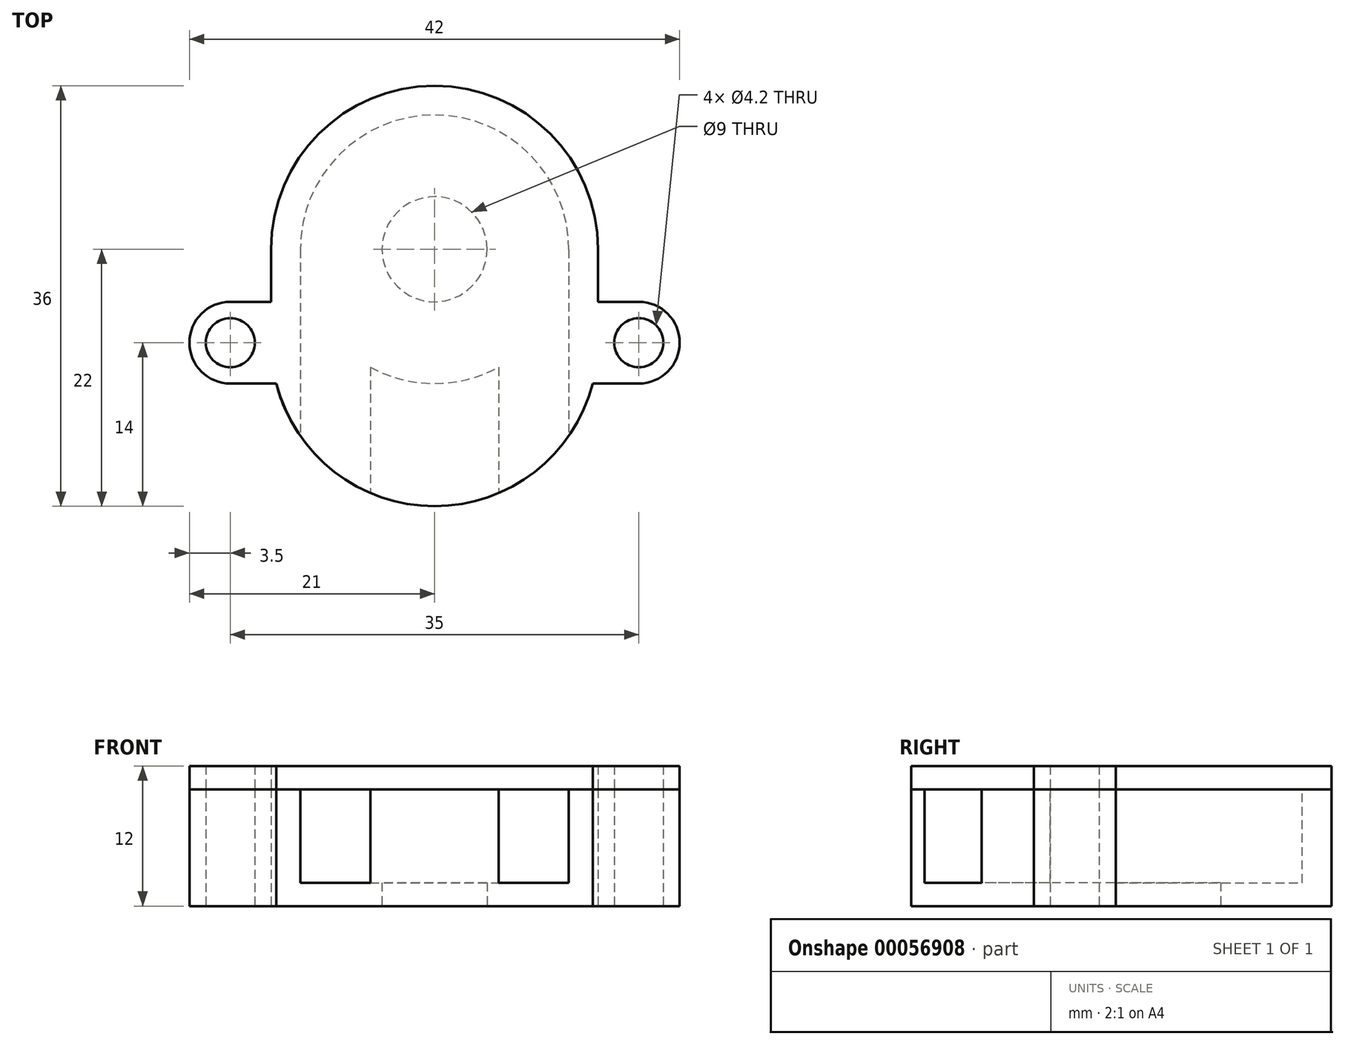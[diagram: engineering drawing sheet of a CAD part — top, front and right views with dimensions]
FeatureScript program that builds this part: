
annotation { "Feature Type Name" : "Feature", "Feature Type Description" : "" }
export const myFeature = defineFeature(function(context is Context, id is Id, definition is map)
    precondition{}
    {
        {
            var Q0;
            Q0=qCreatedBy(makeId("Top.planeOp"),FACE);
            var sketch = newSketch(context, id + "F0", { "sketchPlane" : qUnion([Q0])});
            skArc(sketch, "E0", {"start": v(-13.56, -3.5) * mm, "mid": v(0, -14) * mm, "end": v(13.56, -3.5) * mm});
            skLineSegment(sketch, "E1.rect.bottom", {"start": v(17.5, 3.5) * mm, "end": v(14, 3.5) * mm});
            skLineSegment(sketch, "E1.rect.top", {"start": v(17.5, -3.5) * mm, "end": v(-17.5, -3.5) * mm});
            skLineSegment(sketch, "E1.rect.left", {"start": v(17.5, 3.5) * mm, "end": v(17.5, -3.5) * mm});
            skArc(sketch, "E2", {"start": v(-17.5, 3.5) * mm, "mid": v(-21, 0) * mm, "end": v(-17.5, -3.5) * mm});
            skArc(sketch, "E3", {"start": v(17.5, -3.5) * mm, "mid": v(21, 0) * mm, "end": v(17.5, 3.5) * mm});
            skCircle(sketch, "E4", {"center": v(0, 8) * mm, "radius": 4.5 * mm});
            skArc(sketch, "E5", {"start": v(14, 8) * mm, "mid": v(0, 22) * mm, "end": v(-14, 8) * mm});
            skLineSegment(sketch, "E6", {"start": v(-14, 8) * mm, "end": v(-14, 3.5) * mm});
            skLineSegment(sketch, "E7", {"start": v(14, 8) * mm, "end": v(14, 3.5) * mm});
            skPoint(sketch, "E8.orphan", {"position": v(-14, 0) * mm});
            skLineSegment(sketch, "E9.trimOffspring", {"start": v(-14, 3.5) * mm, "end": v(-17.5, 3.5) * mm});
            skPoint(sketch, "E10.orphan", {"position": v(14, 0) * mm});
            skCircle(sketch, "E11", {"center": v(-17.5, 0) * mm, "radius": 2.1 * mm});
            skCircle(sketch, "E12", {"center": v(17.5, 0) * mm, "radius": 2.1 * mm});
            skSolve(sketch);
        }
        {
            var Q0;
            Q0=qSketchRegion(id+"F0",true);
            extrude(context, id + "F1", {"entities" : qUnion([Q0]), "depth" : 10 * mm});
        }
        {
            var Q0;
            Q0=makeQuery(id+"F1.opExtrude","CAP_FACE",FACE,{"disambiguationData":[OSD([sQuery(id+"F0.wireOp",EDGE,"E0"),sQuery(id+"F0.wireOp",EDGE,"E1.rect.bottom"),sQuery(id+"F0.wireOp",EDGE,"E1.rect.top"),sQuery(id+"F0.wireOp",EDGE,"E2"),sQuery(id+"F0.wireOp",EDGE,"E3"),sQuery(id+"F0.wireOp",EDGE,"E4"),sQuery(id+"F0.wireOp",EDGE,"E5"),sQuery(id+"F0.wireOp",EDGE,"E6"),sQuery(id+"F0.wireOp",EDGE,"E7"),sQuery(id+"F0.wireOp",EDGE,"E9.trimOffspring"),sQuery(id+"F0.wireOp",EDGE,"E11"),sQuery(id+"F0.wireOp",EDGE,"E12")])],"isStart":false});
            var sketch = newSketch(context, id + "F2", { "sketchPlane" : qUnion([Q0])});
            skArc(sketch, "E13", {"start": v(-5.5, -2.1) * mm, "mid": v(0, -3.5) * mm, "end": v(5.5, -2.1) * mm});
            skLineSegment(sketch, "E14.bottom", {"start": v(-11.5, 8) * mm, "end": v(-5.5, 8) * mm});
            skLineSegment(sketch, "E14.top", {"start": v(-11.5, -12.87) * mm, "end": v(-5.5, -12.87) * mm});
            skLineSegment(sketch, "E14.left", {"start": v(-11.5, 8) * mm, "end": v(-11.5, -12.87) * mm});
            skLineSegment(sketch, "E14.right", {"start": v(-5.5, 8) * mm, "end": v(-5.5, -12.87) * mm});
            skLineSegment(sketch, "E15.bottom", {"start": v(11.5, 8) * mm, "end": v(5.5, 8) * mm});
            skLineSegment(sketch, "E15.top", {"start": v(11.5, -12.87) * mm, "end": v(5.5, -12.87) * mm});
            skLineSegment(sketch, "E15.left", {"start": v(11.5, 8) * mm, "end": v(11.5, -12.87) * mm});
            skLineSegment(sketch, "E15.right", {"start": v(5.5, 8) * mm, "end": v(5.5, -12.87) * mm});
            skArc(sketch, "E16.trimOffspring", {"start": v(11.5, 8) * mm, "mid": v(0, 19.5) * mm, "end": v(-11.5, 8) * mm});
            skSolve(sketch);
        }
        {
            var Q0;
            Q0=qSketchRegion(id+"F2",true);
            extrude(context, id + "F3", {"entities" : qUnion([Q0]), "operationType" : NewBodyOperationType.REMOVE, "oppositeDirection" : true, "depth" : 8 * mm});
        }
        {
            var Q0;
            {var subQ0=sQuery(id+"F0.wireOp",EDGE,"E0");var subQ1=sQuery(id+"F0.wireOp",EDGE,"E1.rect.bottom");var subQ2=sQuery(id+"F0.wireOp",EDGE,"E1.rect.top");var subQ3=sQuery(id+"F0.wireOp",EDGE,"E2");var subQ4=sQuery(id+"F0.wireOp",EDGE,"E3");var subQ5=sQuery(id+"F0.wireOp",EDGE,"E5");var subQ6=sQuery(id+"F0.wireOp",EDGE,"E6");var subQ7=sQuery(id+"F0.wireOp",EDGE,"E7");var subQ8=sQuery(id+"F0.wireOp",EDGE,"E9.trimOffspring");var subQ9=sQuery(id+"F0.wireOp",EDGE,"E11");var subQ10=sQuery(id+"F0.wireOp",EDGE,"E12");Q0=makeQuery(id+"F3.boolean.opBoolean","SPLIT",FACE,{"disambiguationData":[TD([makeQuery(id+"F1.opExtrude","SWEPT_FACE",FACE,{"disambiguationData":[OSD([subQ1])]})])],"derivedFrom":makeQuery(id+"F1.opExtrude","CAP_FACE",FACE,{"disambiguationData":[OSD([subQ0,subQ1,subQ2,subQ3,subQ4,sQuery(id+"F0.wireOp",EDGE,"E4"),subQ5,subQ6,subQ7,subQ8,subQ9,subQ10])],"isStart":false})});}
            var sketch = newSketch(context, id + "F4", { "sketchPlane" : qUnion([Q0])});
            skArc(sketch, "E17.0", {"start": v(17.5, -3.5) * mm, "mid": v(21, 0) * mm, "end": v(17.5, 3.5) * mm});
            skLineSegment(sketch, "E17.1", {"start": v(17.5, 3.5) * mm, "end": v(14, 3.5) * mm});
            skLineSegment(sketch, "E17.2", {"start": v(14, 8) * mm, "end": v(14, 3.5) * mm});
            skArc(sketch, "E17.3", {"start": v(14, 8) * mm, "mid": v(0, 22) * mm, "end": v(-14, 8) * mm});
            skLineSegment(sketch, "E17.4", {"start": v(-14, 8) * mm, "end": v(-14, 3.5) * mm});
            skLineSegment(sketch, "E17.5", {"start": v(-14, 3.5) * mm, "end": v(-17.5, 3.5) * mm});
            skArc(sketch, "E17.6", {"start": v(-17.5, 3.5) * mm, "mid": v(-21, 0) * mm, "end": v(-17.5, -3.5) * mm});
            skLineSegment(sketch, "E17.7", {"start": v(-13.56, -3.5) * mm, "end": v(-17.5, -3.5) * mm});
            skArc(sketch, "E17.8", {"start": v(-13.56, -3.5) * mm, "mid": v(-12.73, -5.83) * mm, "end": v(-11.5, -7.98) * mm});
            skArc(sketch, "E17.9", {"start": v(-11.5, -7.98) * mm, "mid": v(-8.84, -10.85) * mm, "end": v(-5.5, -12.87) * mm});
            skArc(sketch, "E17.10", {"start": v(-5.5, -12.87) * mm, "mid": v(0, -14) * mm, "end": v(5.5, -12.87) * mm});
            skArc(sketch, "E17.11", {"start": v(5.5, -12.87) * mm, "mid": v(8.84, -10.85) * mm, "end": v(11.5, -7.98) * mm});
            skArc(sketch, "E17.12", {"start": v(11.5, -7.98) * mm, "mid": v(12.73, -5.83) * mm, "end": v(13.56, -3.5) * mm});
            skLineSegment(sketch, "E17.13", {"start": v(17.5, -3.5) * mm, "end": v(13.56, -3.5) * mm});
            skCircle(sketch, "E18.0", {"center": v(-17.5, 0) * mm, "radius": 2.1 * mm});
            skCircle(sketch, "E19.0", {"center": v(17.5, 0) * mm, "radius": 2.1 * mm});
            skSolve(sketch);
        }
        {
            var Q0;
            Q0=qSketchRegion(id+"F4",true);
            extrude(context, id + "F5", {"entities" : qUnion([Q0]), "depth" : 2 * mm});
        }
    });
